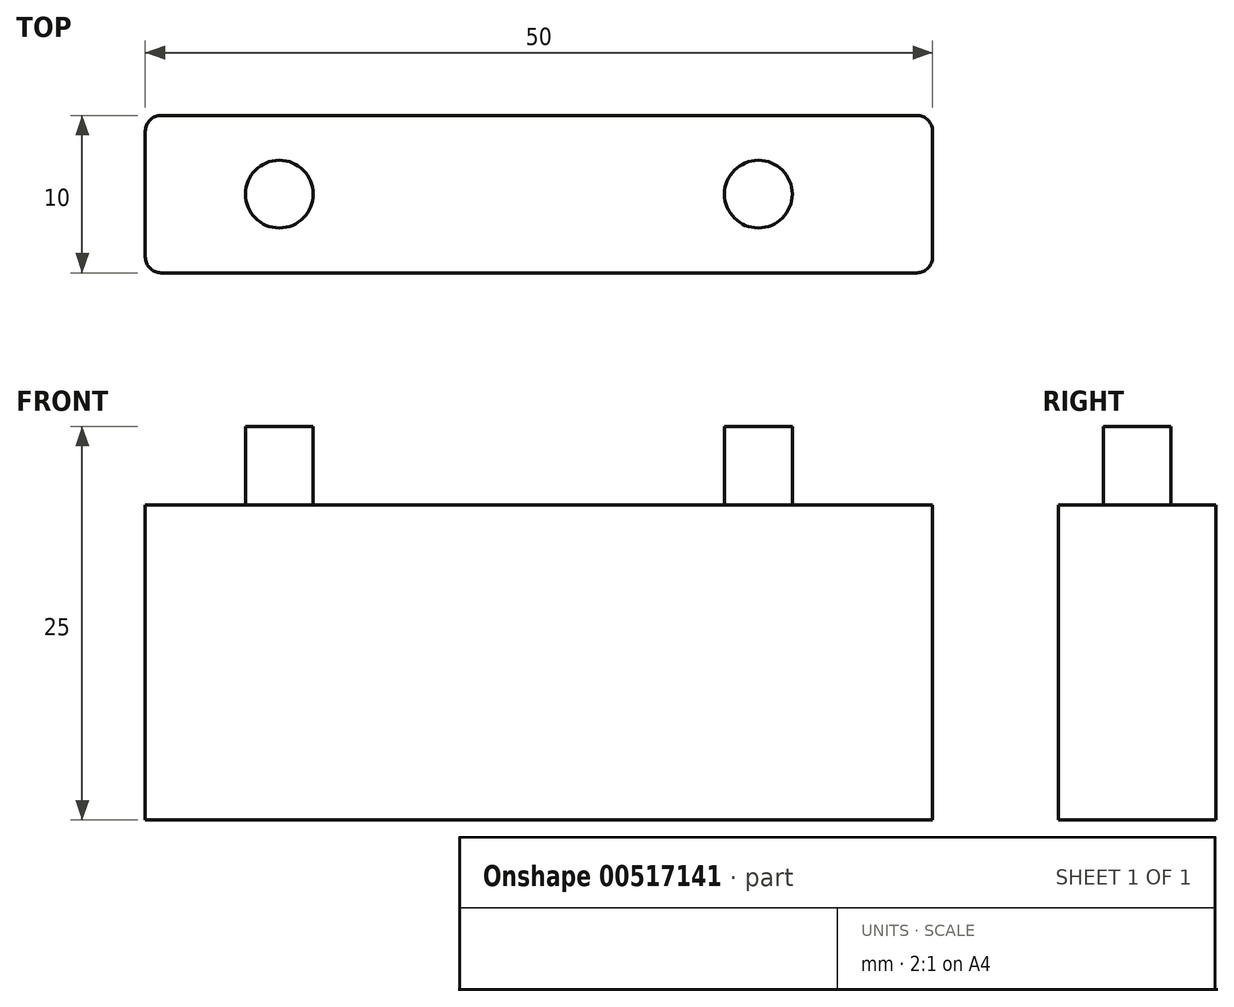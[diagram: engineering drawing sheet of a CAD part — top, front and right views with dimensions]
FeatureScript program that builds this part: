
annotation { "Feature Type Name" : "Feature", "Feature Type Description" : "" }
export const myFeature = defineFeature(function(context is Context, id is Id, definition is map)
    precondition{}
    {
        {
            var Q0;
            Q0=qCreatedBy(makeId("Top.planeOp"),FACE);
            var sketch = newSketch(context, id + "F0", { "sketchPlane" : qUnion([Q0])});
            skLineSegment(sketch, "E0.bottom", {"start": v(-16.2, 19.23) * mm, "end": v(33.8, 19.23) * mm});
            skLineSegment(sketch, "E0.top", {"start": v(-16.2, 9.23) * mm, "end": v(33.8, 9.23) * mm});
            skLineSegment(sketch, "E0.left", {"start": v(-16.2, 19.23) * mm, "end": v(-16.2, 9.23) * mm});
            skLineSegment(sketch, "E0.right", {"start": v(33.8, 19.23) * mm, "end": v(33.8, 9.23) * mm});
            skSolve(sketch);
        }
        {
            var Q0;
            Q0=makeQuery(id+"F0.imprint","IMPRINT",FACE,{"disambiguationData":[TD([[makeQuery(id+"F0.imprint","IMPRINT",EDGE,{"derivedFrom":sQuery(id+"F0.wireOp",EDGE,"E0.bottom")}),-1.0]])]});
            extrude(context, id + "F1", {"entities" : qUnion([Q0]), "depth" : 20 * mm, "offsetDistance" : 25 * mm});
        }
        {
            var Q0;
            Q0=makeQuery(id+"F1.opExtrude","CAP_FACE",FACE,{"disambiguationData":[OSD([sQuery(id+"F0.wireOp",EDGE,"E0.bottom"),sQuery(id+"F0.wireOp",EDGE,"E0.top"),sQuery(id+"F0.wireOp",EDGE,"E0.left"),sQuery(id+"F0.wireOp",EDGE,"E0.right")])],"isStart":false});
            var sketch = newSketch(context, id + "F2", { "sketchPlane" : qUnion([Q0])});
            skCircle(sketch, "E1", {"center": v(-7.7, 14.23) * mm, "radius": 2.15 * mm});
            skCircle(sketch, "E2", {"center": v(22.73, 14.23) * mm, "radius": 2.15 * mm});
            skSolve(sketch);
        }
        {
            var Q0;
            Q0=makeQuery(id+"F2.imprint","IMPRINT",FACE,{"disambiguationData":[TD([[makeQuery(id+"F2.imprint","IMPRINT",EDGE,{"derivedFrom":sQuery(id+"F2.wireOp",EDGE,"E1")}),1.0]])]});
            var Q1;
            Q1=makeQuery(id+"F2.imprint","IMPRINT",FACE,{"disambiguationData":[TD([[makeQuery(id+"F2.imprint","IMPRINT",EDGE,{"derivedFrom":sQuery(id+"F2.wireOp",EDGE,"E2")}),1.0]])]});
            extrude(context, id + "F3", {"entities" : qUnion([Q0, Q1]), "operationType" : NewBodyOperationType.ADD, "depth" : 5 * mm, "offsetDistance" : 25 * mm});
        }
        {
            var Q0;
            Q0=makeQuery(id+"F1.opExtrude","SWEPT_EDGE",EDGE,{"disambiguationData":[OSD([sQuery(id+"F0.wireOp",EDGE,"E0.top"),sQuery(id+"F0.wireOp",EDGE,"E0.right")])]});
            var Q1;
            Q1=makeQuery(id+"F1.opExtrude","SWEPT_EDGE",EDGE,{"disambiguationData":[OSD([sQuery(id+"F0.wireOp",EDGE,"E0.bottom"),sQuery(id+"F0.wireOp",EDGE,"E0.right")])]});
            var Q2;
            Q2=makeQuery(id+"F1.opExtrude","SWEPT_EDGE",EDGE,{"disambiguationData":[OSD([sQuery(id+"F0.wireOp",EDGE,"E0.top"),sQuery(id+"F0.wireOp",EDGE,"E0.left")])]});
            var Q3;
            Q3=makeQuery(id+"F1.opExtrude","SWEPT_EDGE",EDGE,{"disambiguationData":[OSD([sQuery(id+"F0.wireOp",EDGE,"E0.bottom"),sQuery(id+"F0.wireOp",EDGE,"E0.left")])]});
            fillet(context, id + "F4", {"entities" : qUnion([Q0, Q1, Q2, Q3]), "radius" : 1 * mm, "tangentPropagation" : true, "allowEdgeOverflow" : false});
        }
    });
